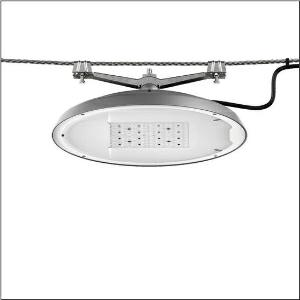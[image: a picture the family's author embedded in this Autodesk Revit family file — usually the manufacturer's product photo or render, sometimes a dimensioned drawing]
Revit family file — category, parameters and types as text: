
# Revit family: dl_r__50_iq_mini___st0_8s_5xa248v41f08me_8e0e
name_source: partatom
category: Lighting Fixtures
units: mm (PartAtom-declared; Revit-internal decimal feet)

## family parameters
Cut with Voids When Loaded = No
Host = Face
Light Source = No
Part Type = Normal
Room Calculation Point = No
Round Connector Dimension = Use Diameter
Shared = No

## types (1)
- --- (1 x LED, 15660 lm, 101.7 W, 4000K)
    Apparent Load = 102 VA
    CIE Flux Codes = 38 75 97 100 100
    Color Rendering = 70
    Color Temperature = 4000K
    Default Elevation = 1800 mm
    Description = DL® 50 iQ mini, catenary luminaire, primary light control with lens, of PMMA, primary optical cover: cover, of toughened safety glass, transparent, light distribution: ST0.8s, light emission: direct distribution, primary light characteristic: symmetric, installation type: suspended mounting, LED, High Power LED, rated luminous flux: 15.660lm, luminous efficacy: 154lm/W, light colour: 740, colour temperature: 4000K, control: optimised constant luminous flux control (CLO 2.0), Desk-Remote (wireless, voltage-free reading and setting of iQ features in the workshop via application-optimized NFC function/RFID function), Light-Fading, Smart-Wire, Night-Set, Lumen-Switch, Temp-Guard, Auto-Match, Street-Remote, mains connection: 230..240V, AC, 50/60Hz, start of lifetime: 102W, end of service life: 111W, reduction: 45W, luminaire housing, of diecast aluminium, powder-coated, Siteco® metallic grey (DB 702S), diameter: 500mm, height: 115mm, protection rating (complete): IP66, insulation class (complete): insulation class II (safety insulation), certification: CE, ENEC, VDE, impact resistance: IK08, permissible operating ambient temperature for outdoor applications: -25..+40°C, standard-compliant lighting for roads and squares, packaging unit: 1 piece

Light Distribution: ST0.8s
    Height = 124 mm  [stored 0.406824 ft]
    Lamp = 1 x LED
    Lamp Light Flux = 15660 lm
    Lamp Power = 101.7 W
    Lamp count = 1
    Length = 500 mm
    Luminous efficacy = 154 lm/W
    Manufacturer = Siteco
    ModVariant = No
    Model = 5XA248V41F08ME
    Number of Poles = 1
    OnlyDefault = Yes
    Power Factor = 1
    Product Name = DL® 50 iQ mini | ST0.8s
    Product group = catenary luminaire
    ProductGroupID = 6300
    Protection Class = Protection class II
    Protection Degree = IP 66
    RLX_Detail_Level = 1
    RLX_Emergency_Light_Flux = 0 lm
    RLX_Emergency_Type = 0
    RLX_Emergency_Type_DB = No
    RlxData = <blob elided: 127449 chars, md5=5a5bed6c>
    Socket = socket
    Standby Power = 0 W
    System Light Flux = 15660 lm
    System Power = 102 W
    Type Comments = factory setting: luminous flux: 100 % | dim-lin: 254 | 534 mA
    Type Image = l_1251783.jpg
    URL = http://relux.com
    VarID = @adj_090313
    Voltage = 0 V
    Weight = 0.00 kg
    Width = 0 mm  [stored 0 ft]

note: [stored X ft] marks values corroborated as IEEE doubles in the binary element streams (Revit-internal decimal feet)

## geometry (parser evidence)
native form markers: Blend x4, Sweep x15
no freeform markers — native parametric forms only
